# Revit family: 0004886 Feilo Sylvania Lighting Fixture START TRACK SPOT S 24W 3K RA90 NB BLACK
name_source: partatom
category: Lighting Fixtures
revit_build: Autodesk Revit 2017 (Build: 20190507_1515(x64)
units: mm (PartAtom-declared; Revit-internal decimal feet)

## family parameters
Cut with Voids When Loaded = No
Host = Face
Light Source = No
OmniClass Number = 23.80.70.00
OmniClass Title = Lighting
Part Type = Normal
Room Calculation Point = No
Round Connector Dimension = Use Diameter
Shared = No

## types (1)
- 0004886 START TRACK SPOT S 24W 3K RA90 NB BLACK
    Apparent Load = 24 VA
    Assembly Code = D5020200
    AssetType = Fixed
    ClassificationName = Uniclass2015
    ClassificationValue = EF_70_80
    Cost = 0 $
    Default Elevation = 1219 mm
    Description = Integrated LED spotlight, Textured Black - RAL9005, compact and minimalist design, ideal for retail applications, die-cast aluminium body, passive cooling heatsink. Beam angle: 12°, color temperature: 3000K , total system power: 24W, total fixture output: 1987 lm, LOR: 100%, colour rendering: Ra: 90 typical, LED Chromaticity: 3 step MacAdam ellipse, lifetime: >50000 hours at L70B50, energy class: A++, A+, A, IR/UV free light source without heat radiation, operating voltage: 220-240V / 50-60Hz, drive current: 600mA, electronic driver, non-dimmable, power factor: 0.95, electrical protection: Class II, Global Track 3 Phase adapter suitable for Global trac 3-circuit tracks, ingress protection rating: IP20, suitable for internal environment only, horizontal rotation: 355°, vertical tilt: 90°, dimensions: Ø86x140x200, weight: 0.966kg.
    DimmingControlOptions = Non dimmable
    DocumentationLiterature = http://www.sylvania-lighting.com
    DurationUnit = hours
    ElectricShockClassification = Class II
    ExpectedLife = 50000
    IfcExportAs = IfcLightFixtureType
    IfcExportType = IfcLightFixtureType
    ImpactProtectionIndex = IK02
    IngressProtection = IP20
    InputNominalFrequency = 50/60 Hz
    InputVoltage = 230-240V~
    Keynote = 16500
    Lamp = LED
    LampColourRenderingIndex = 90
    LampColourTemperature = 3000 K
    LampMacAdamStep = 3
    LampNominalLuminous = 1987 lm
    LampsType = LED
    LightOutputRatio = 100
    LuminousEfficacy = 83 lm/W
    Manufacturer = Feilo Sylvania
    ManufacturerName = Feilo Sylvania
    Material = adc12 aluminium housing, polycarbonate diffuser
    Material_1_FEILO = Body-Sylvania-StartTrackSpot-Black
    Material_2_FEILO = <By Category>
    Material_3_FEILO = <By Category>
    Material_4_FEILO = <By Category>
    Model = START TRACK SPOT S 24W 3K RA90 NB BLACK
    ModelNumber = 0004886
    ModelReference = START TRACK SPOT S 24W 3K RA90 NB BLACK
    Name = START TRACK SPOT S 24W 3K RA90 NB BLACK
    NominalDepth = 140 mm
    NominalHeight = 200 mm  [stored 0.656168 ft]
    NominalLength = 0 mm  [stored 0 ft]
    PowerConsumption = 24 W
    PowerFactor = 0.95
    Type Image = <None>
    TypeBox_FEILO = Start Track Spot Box : Type Small Black
    TypeHead_FEILO = Start Track Spot Head : 0004886 START TRACK SPOT S 24W 3K RA90 NB BLACK
    TypeName = START TRACK SPOT S 24W 3K RA90 NB BLACK
    URL = http://www.sylvania-lighting.com
    Voltage = 230 V
    Weight = 0.966 kg

note: [stored X ft] marks values corroborated as IEEE doubles in the binary element streams (Revit-internal decimal feet)

## geometry (parser evidence)
native form markers: Sweep x5
no freeform markers — native parametric forms only
